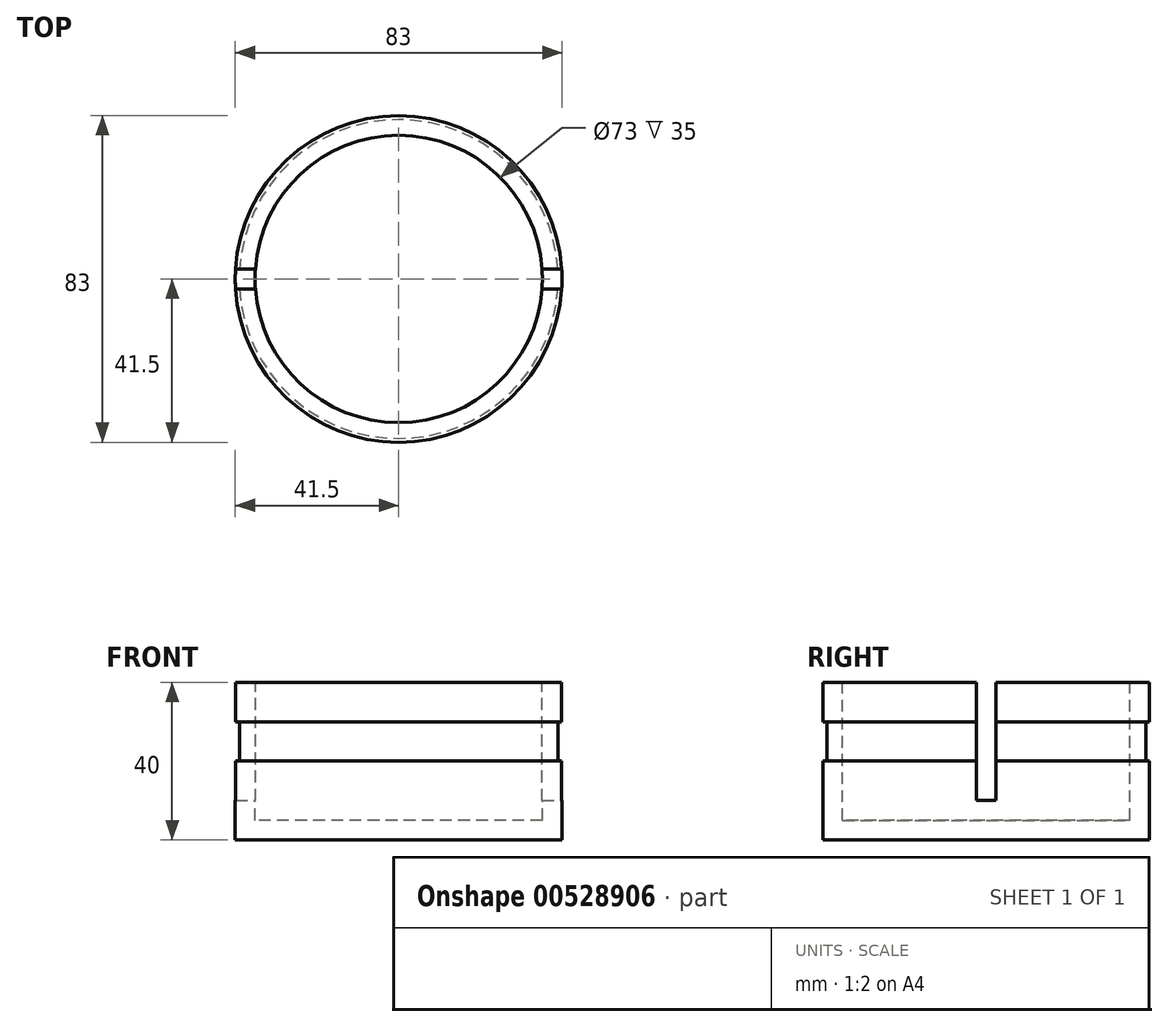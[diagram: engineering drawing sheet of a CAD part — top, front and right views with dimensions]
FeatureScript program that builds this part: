
annotation { "Feature Type Name" : "Feature", "Feature Type Description" : "" }
export const myFeature = defineFeature(function(context is Context, id is Id, definition is map)
    precondition{}
    {
        {
            var Q0;
            Q0=qCreatedBy(makeId("Front.planeOp"),FACE);
            var sketch = newSketch(context, id + "F0", { "sketchPlane" : qUnion([Q0])});
            skLineSegment(sketch, "E0", {"start": v(0, 0) * mm, "end": v(41.5, 0) * mm});
            skLineSegment(sketch, "E1", {"start": v(41.5, 0) * mm, "end": v(41.5, 20) * mm});
            skLineSegment(sketch, "E2", {"start": v(41.5, 20) * mm, "end": v(40.5, 20) * mm});
            skLineSegment(sketch, "E3", {"start": v(40.5, 20) * mm, "end": v(40.5, 30) * mm});
            skLineSegment(sketch, "E4", {"start": v(40.5, 30) * mm, "end": v(41.5, 30) * mm});
            skLineSegment(sketch, "E5", {"start": v(41.5, 30) * mm, "end": v(41.5, 40) * mm});
            skLineSegment(sketch, "E6", {"start": v(41.5, 40) * mm, "end": v(36.5, 40) * mm});
            skLineSegment(sketch, "E7", {"start": v(36.5, 40) * mm, "end": v(36.5, 5) * mm});
            skLineSegment(sketch, "E8", {"start": v(36.5, 5) * mm, "end": v(0, 5) * mm});
            skLineSegment(sketch, "E9", {"start": v(0, 5) * mm, "end": v(0, 0) * mm});
            skSolve(sketch);
        }
        {
            var Q0;
            Q0 = qSketchRegion(id + "F0", true);
            var Q1;
            Q1=sQuery(id+"F0.wireOp",EDGE,"E9");
            revolve(context, id + "F1", {"entities" : qUnion([Q0]), "axis" : qUnion([Q1]), "revolveType" : RevolveType.FULL});
        }
        {
            var Q0;
            Q0=makeQuery(id+"F1.opRevolve","SWEPT_FACE",FACE,{"disambiguationData":[OSD([sQuery(id+"F0.wireOp",EDGE,"E6")])]});
            var sketch = newSketch(context, id + "F2", { "sketchPlane" : qUnion([Q0])});
            skLineSegment(sketch, "E10.bottom", {"start": v(-50, -2.5) * mm, "end": v(50, -2.5) * mm});
            skLineSegment(sketch, "E10.top", {"start": v(-50, 2.5) * mm, "end": v(50, 2.5) * mm});
            skLineSegment(sketch, "E10.left", {"start": v(-50, -2.5) * mm, "end": v(-50, 2.5) * mm});
            skLineSegment(sketch, "E10.right", {"start": v(50, -2.5) * mm, "end": v(50, 2.5) * mm});
            skPoint(sketch, "E10.middle", {"position": v(0, 0) * mm});
            skSolve(sketch);
        }
        {
            var Q0;
            Q0 = qSketchRegion(id + "F2", true);
            extrude(context, id + "F3", {"entities" : qUnion([Q0]), "operationType" : NewBodyOperationType.REMOVE, "oppositeDirection" : true, "depth" : 30 * mm, "offsetDistance" : 25 * mm});
        }
    });
